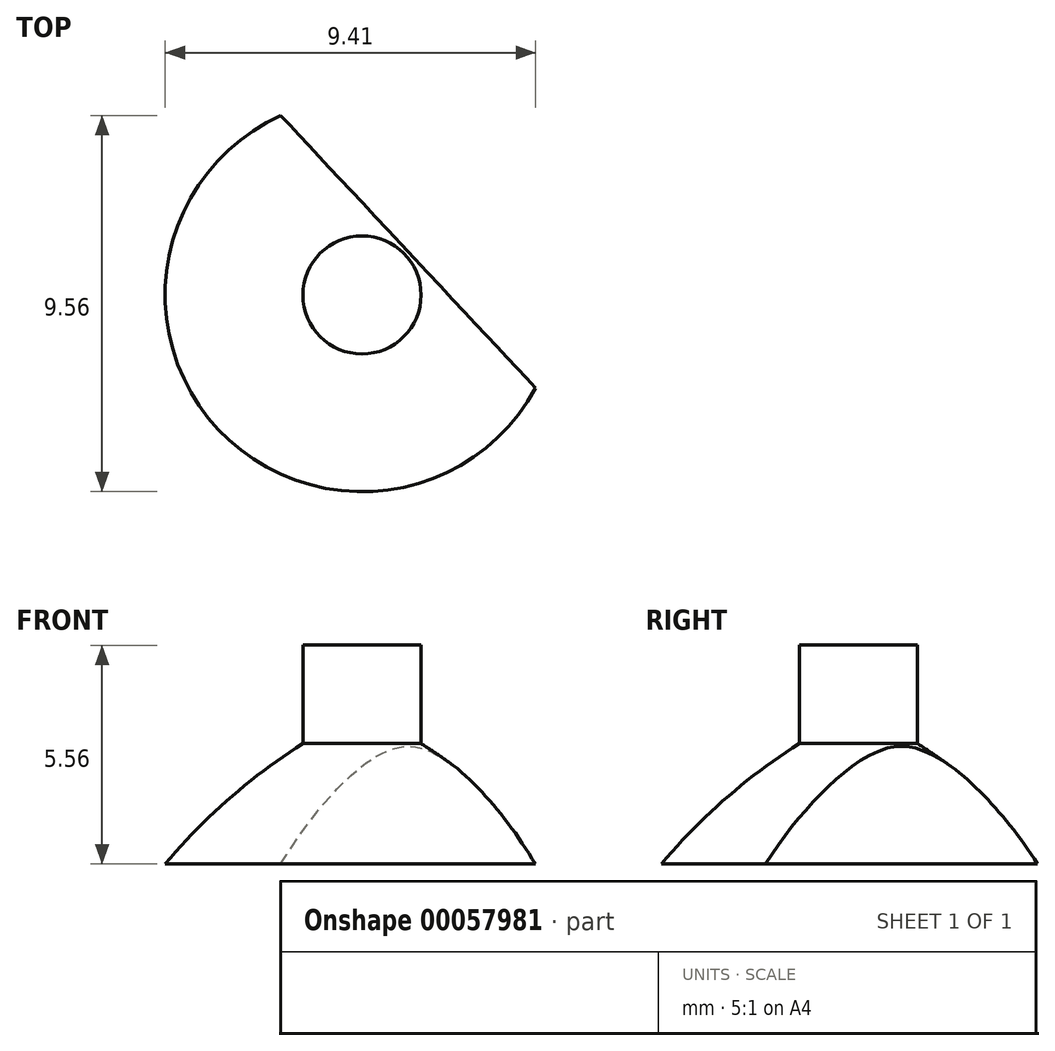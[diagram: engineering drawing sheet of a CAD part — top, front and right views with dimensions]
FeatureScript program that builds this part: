
annotation { "Feature Type Name" : "Feature", "Feature Type Description" : "" }
export const myFeature = defineFeature(function(context is Context, id is Id, definition is map)
    precondition{}
    {
        {
            var Q0;
            Q0=qCreatedBy(makeId("Front.planeOp"),FACE);
            var sketch = newSketch(context, id + "F0", { "sketchPlane" : qUnion([Q0])});
            skLineSegment(sketch, "E0", {"start": v(0, 0) * mm, "end": v(0, 5.56) * mm});
            skLineSegment(sketch, "E1", {"start": v(0, 5.56) * mm, "end": v(-1.5, 5.56) * mm});
            skLineSegment(sketch, "E2", {"start": v(-1.5, 5.56) * mm, "end": v(-1.5, 3.06) * mm});
            skArc(sketch, "E3", {"start": v(-1.5, 3.06) * mm, "mid": v(-3.37, 1.67) * mm, "end": v(-5, 0) * mm});
            skLineSegment(sketch, "E4", {"start": v(-5, 0) * mm, "end": v(0, 0) * mm});
            skSolve(sketch);
        }
        {
            var Q0;
            Q0 = qSketchRegion(id + "F0", true);
            var Q1;
            Q1=sQuery(id+"F0.wireOp",EDGE,"E0");
            revolve(context, id + "F1", {"entities" : qUnion([Q0]), "axis" : qUnion([Q1]), "revolveType" : RevolveType.FULL});
        }
        {
            var Q0;
            Q0=qCreatedBy(makeId("Top.planeOp"),FACE);
            var sketch = newSketch(context, id + "F2", { "sketchPlane" : qUnion([Q0])});
            skLineSegment(sketch, "E5", {"start": v(-2.84, 5.4) * mm, "end": v(6.05, -4.1) * mm});
            skLineSegment(sketch, "E6", {"start": v(6.05, -4.1) * mm, "end": v(7.3, 7.12) * mm});
            skLineSegment(sketch, "E7", {"start": v(7.3, 7.12) * mm, "end": v(-2.84, 5.4) * mm});
            skSolve(sketch);
        }
        {
            var Q0;
            Q0 = qSketchRegion(id + "F2", true);
            extrude(context, id + "F3", {"entities" : qUnion([Q0]), "operationType" : NewBodyOperationType.REMOVE, "endBound" : BoundingType.THROUGH_ALL, "depth" : 25 * mm});
        }
    });
